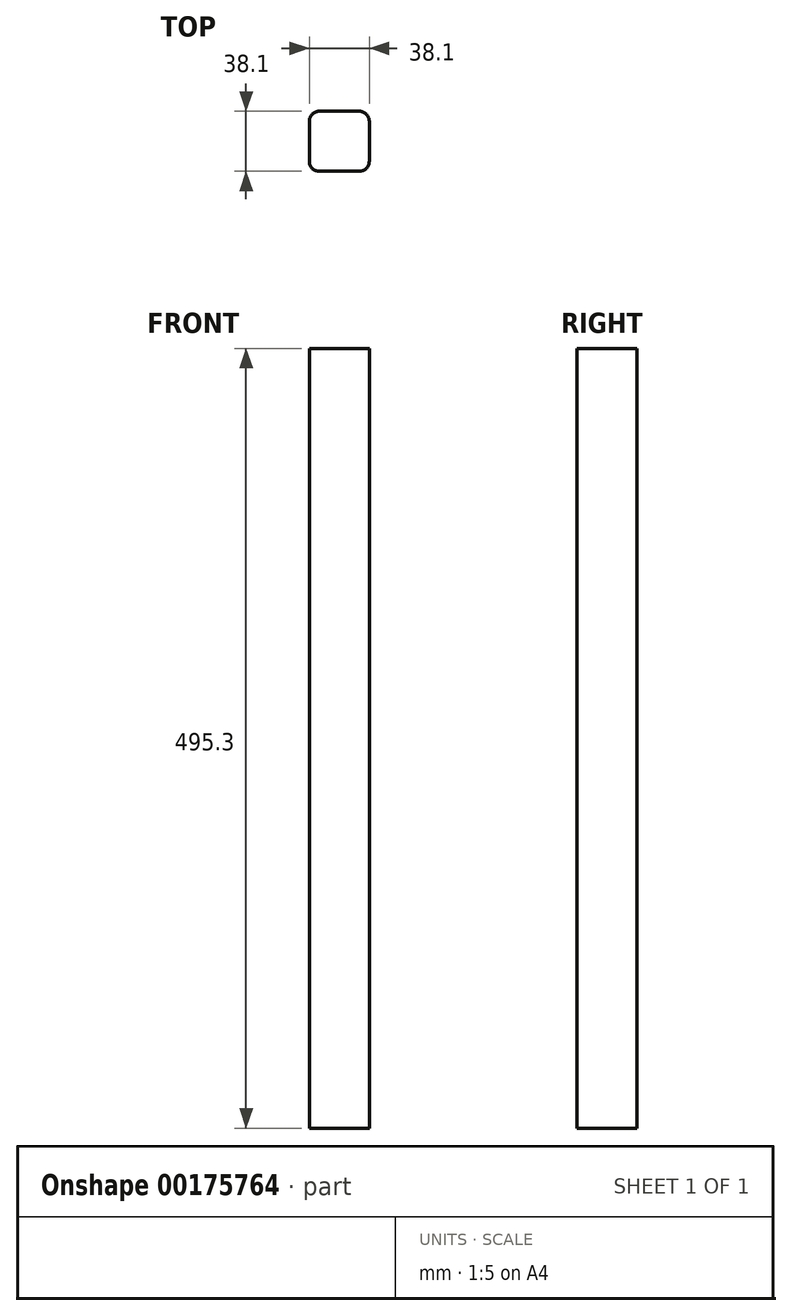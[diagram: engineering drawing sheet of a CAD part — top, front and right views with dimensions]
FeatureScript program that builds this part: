
annotation { "Feature Type Name" : "Feature", "Feature Type Description" : "" }
export const myFeature = defineFeature(function(context is Context, id is Id, definition is map)
    precondition{}
    {
        {
            var Q0;
            Q0=qCreatedBy(makeId("Top.planeOp"),FACE);
            var sketch = newSketch(context, id + "F0", { "sketchPlane" : qUnion([Q0])});
            skLineSegment(sketch, "E0.bottom", {"start": v(12.7, 19.05) * mm, "end": v(-12.7, 19.05) * mm});
            skLineSegment(sketch, "E0.top", {"start": v(12.7, -19.05) * mm, "end": v(-12.7, -19.05) * mm});
            skLineSegment(sketch, "E0.left", {"start": v(19.05, 12.7) * mm, "end": v(19.05, -12.7) * mm});
            skLineSegment(sketch, "E0.right", {"start": v(-19.05, 12.7) * mm, "end": v(-19.05, -12.7) * mm});
            skPoint(sketch, "E0.middle", {"position": v(0, 0) * mm});
            skPoint(sketch, "E1.visualSharp", {"position": v(-19.05, 19.05) * mm});
            skPoint(sketch, "E2.visualSharp", {"position": v(19.05, 19.05) * mm});
            skArc(sketch, "E2.filletArc", {"start": v(19.05, 12.7) * mm, "mid": v(17.2, 17.2) * mm, "end": v(12.7, 19.05) * mm});
            skPoint(sketch, "E3.visualSharp", {"position": v(19.05, -19.05) * mm});
            skArc(sketch, "E3.filletArc", {"start": v(12.7, -19.05) * mm, "mid": v(17.2, -17.2) * mm, "end": v(19.05, -12.7) * mm});
            skPoint(sketch, "E4.visualSharp", {"position": v(-19.05, -19.05) * mm});
            skArc(sketch, "E4.filletArc", {"start": v(-19.05, -12.7) * mm, "mid": v(-17.2, -17.2) * mm, "end": v(-12.7, -19.05) * mm});
            skArc(sketch, "E5.filletArc", {"start": v(-12.7, 19.05) * mm, "mid": v(-17.2, 17.2) * mm, "end": v(-19.05, 12.7) * mm});
            skSolve(sketch);
        }
        {
            var Q0;
            Q0=makeQuery(id+"F0.imprint","IMPRINT",FACE,{"disambiguationData":[TD([[makeQuery(id+"F0.imprint","IMPRINT",EDGE,{"derivedFrom":sQuery(id+"F0.wireOp",EDGE,"E0.bottom")}),1.0]])]});
            extrude(context, id + "F1", {"entities" : qUnion([Q0]), "depth" : 495.3 * mm});
        }
    });
